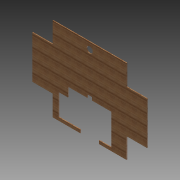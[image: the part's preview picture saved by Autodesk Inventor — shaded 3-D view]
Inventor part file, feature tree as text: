
AUTODESK INVENTOR PART (.ipt)
format: ipt  version: 2012 (Build 160160000, 160)  size: 126,464 bytes
history: native  units: in
note: dims shown in document units (in); Inventor stores cm internally (conversion verified against a paired STEP export)
features: extrude x1, sketch x1
ambient origin geometry x8: Origin, YZ Plane, XZ Plane, XY Plane, X Axis, Y Axis, Z Axis, Center Point
bodies: Solid1 (feature_tree)
feature tree (2):
  extrude  "Extrusion1"  Depth=27.0in
  sketch  "Sketch1"  dims[d0=37.0in d1=27.0in d2=23.75in d3=13.75in d4=6.625in d5=6.625in d6=6.625in d8=6.625in d9=0.25in d10=0.0in d11=6.0in d12=8.875in d13=8.875in d14=1.0in d15=14.0in d17=1.0in d18=1.5in d19=2.0in d20=2.25in d21=10.0in d22=4.875in d23=4.875in d24=3.0in d25=7.0in]
